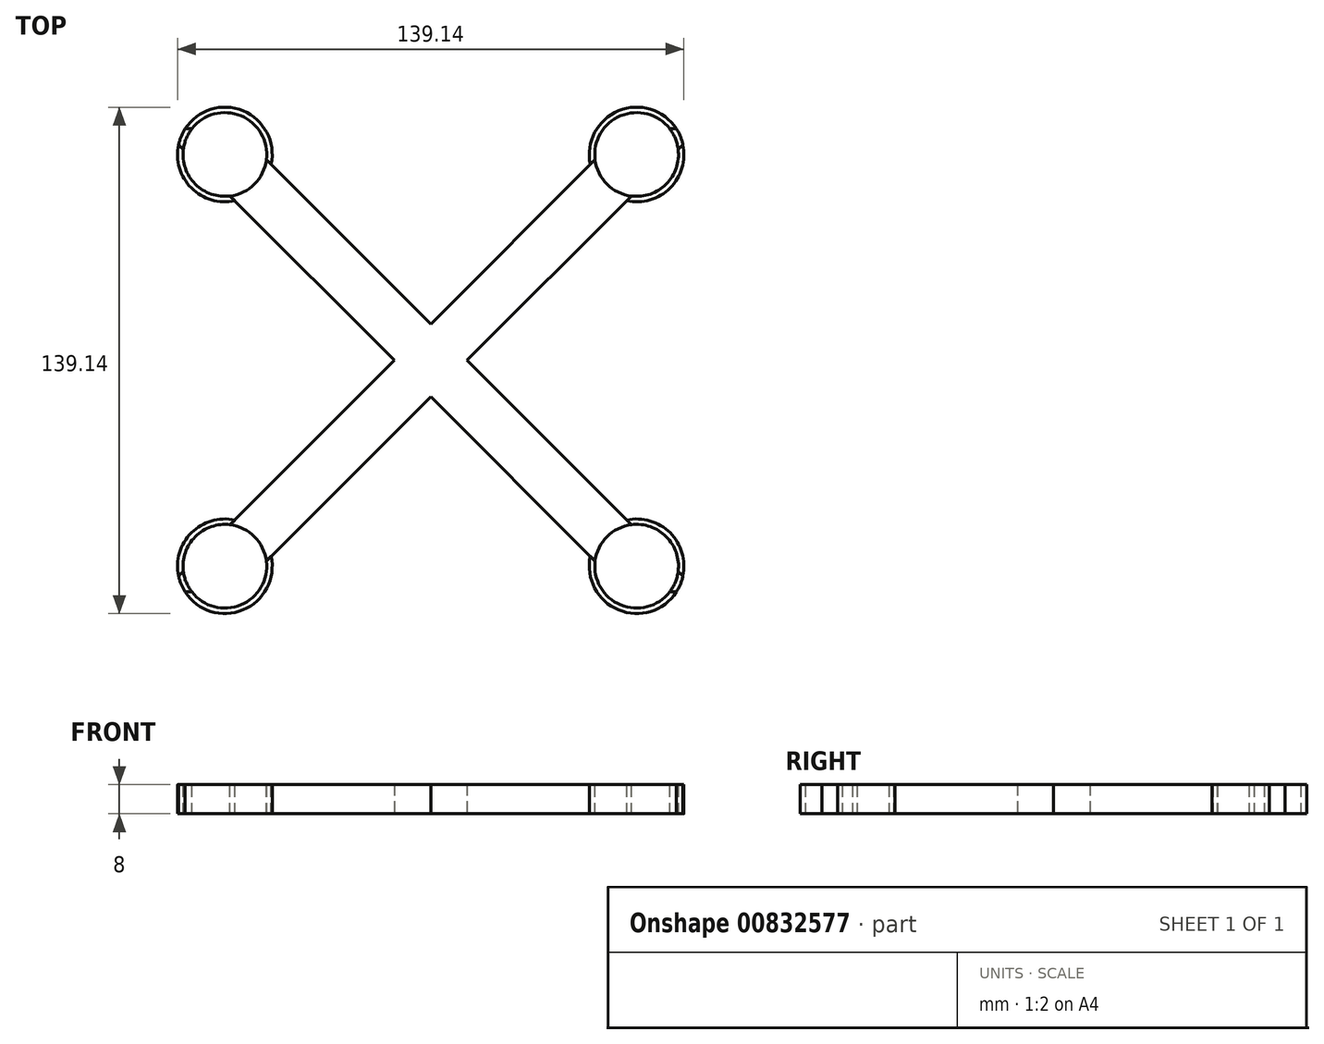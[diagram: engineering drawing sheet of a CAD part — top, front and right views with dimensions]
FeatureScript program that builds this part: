
annotation { "Feature Type Name" : "Feature", "Feature Type Description" : "" }
export const myFeature = defineFeature(function(context is Context, id is Id, definition is map)
    precondition{}
    {
        {
            var Q0;
            Q0=qCreatedBy(makeId("Top.planeOp"),FACE);
            var sketch = newSketch(context, id + "F0", { "sketchPlane" : qUnion([Q0])});
            skLineSegment(sketch, "E0", {"start": v(0, 0) * mm, "end": v(127.28, 127.28) * mm, "construction": true});
            skLineSegment(sketch, "E1", {"start": v(0, 127.28) * mm, "end": v(127.28, 0) * mm, "construction": true});
            skLineSegment(sketch, "E2", {"start": v(-10, 127.28) * mm, "end": v(10, 127.28) * mm});
            skLineSegment(sketch, "E3", {"start": v(117.28, 0) * mm, "end": v(137.28, 0) * mm});
            skLineSegment(sketch, "E4", {"start": v(10, 127.28) * mm, "end": v(137.28, 0) * mm});
            skLineSegment(sketch, "E5", {"start": v(117.28, 0) * mm, "end": v(-10, 127.28) * mm});
            skLineSegment(sketch, "E6", {"start": v(117.28, 127.28) * mm, "end": v(137.28, 127.28) * mm});
            skLineSegment(sketch, "E7", {"start": v(-10, 0) * mm, "end": v(10, 0) * mm});
            skLineSegment(sketch, "E8", {"start": v(-10, 0) * mm, "end": v(117.28, 127.28) * mm});
            skLineSegment(sketch, "E9", {"start": v(137.28, 127.28) * mm, "end": v(10, 0) * mm});
            skSolve(sketch);
        }
        {
            var Q0;
            {var subQ0=sQuery(id+"F0.wireOp",EDGE,"E2");Q0=makeQuery(id+"F0.imprint","IMPRINT",FACE,{"disambiguationData":[TD([[makeQuery(id+"F0.imprint","IMPRINT",EDGE,{"derivedFrom":subQ0}),-1.0]])]});}
            var Q1;
            {var subQ0=sQuery(id+"F0.wireOp",EDGE,"E8");var subQ1=sQuery(id+"F0.wireOp",EDGE,"E4");var subQ2=makeQuery(id+"F0.imprint","INTERSECT",VERTEX,{"derivedFrom":[subQ1,subQ0]});Q1=makeQuery(id+"F0.imprint","IMPRINT",FACE,{"disambiguationData":[TD([[makeQuery(id+"F0.imprint","IMPRINT",EDGE,{"disambiguationData":[TD([[subQ2,-1.0]])],"derivedFrom":subQ1}),-1.0]])]});}
            var Q2;
            {var subQ5=sQuery(id+"F0.wireOp",EDGE,"E6");Q2=makeQuery(id+"F0.imprint","IMPRINT",FACE,{"disambiguationData":[TD([[makeQuery(id+"F0.imprint","IMPRINT",EDGE,{"derivedFrom":subQ5}),-1.0]])]});}
            var Q3;
            {var subQ0=sQuery(id+"F0.wireOp",EDGE,"E3");Q3=makeQuery(id+"F0.imprint","IMPRINT",FACE,{"disambiguationData":[TD([[makeQuery(id+"F0.imprint","IMPRINT",EDGE,{"derivedFrom":subQ0}),1.0]])]});}
            var Q4;
            {var subQ5=sQuery(id+"F0.wireOp",EDGE,"E7");Q4=makeQuery(id+"F0.imprint","IMPRINT",FACE,{"disambiguationData":[TD([[makeQuery(id+"F0.imprint","IMPRINT",EDGE,{"derivedFrom":subQ5}),1.0]])]});}
            extrude(context, id + "F1", {"entities" : qUnion([Q0, Q1, Q2, Q3, Q4]), "depth" : 8 * mm, "offsetDistance" : 25 * mm});
        }
        {
            var Q0;
            Q0=makeQuery(id+"F1.opExtrude","CAP_FACE",FACE,{"disambiguationData":[OSD([sQuery(id+"F0.wireOp",EDGE,"E2"),sQuery(id+"F0.wireOp",EDGE,"E3"),sQuery(id+"F0.wireOp",EDGE,"E4"),sQuery(id+"F0.wireOp",EDGE,"E5"),sQuery(id+"F0.wireOp",EDGE,"E6"),sQuery(id+"F0.wireOp",EDGE,"E7"),sQuery(id+"F0.wireOp",EDGE,"E8"),sQuery(id+"F0.wireOp",EDGE,"E9")])],"isStart":false});
            var sketch = newSketch(context, id + "F2", { "sketchPlane" : qUnion([Q0])});
            skCircle(sketch, "E10", {"center": v(7.07, 7.07) * mm, "radius": 11.5 * mm});
            skCircle(sketch, "E11", {"center": v(120.2, 7.07) * mm, "radius": 11.5 * mm});
            skCircle(sketch, "E12", {"center": v(120.2, 120.2) * mm, "radius": 11.5 * mm});
            skCircle(sketch, "E13", {"center": v(7.07, 120.2) * mm, "radius": 11.5 * mm});
            skCircle(sketch, "E14", {"center": v(120.2, 120.2) * mm, "radius": 13 * mm});
            skCircle(sketch, "E15", {"center": v(120.2, 7.07) * mm, "radius": 13 * mm});
            skCircle(sketch, "E16", {"center": v(7.07, 7.07) * mm, "radius": 13 * mm});
            skCircle(sketch, "E17", {"center": v(7.07, 120.2) * mm, "radius": 13 * mm});
            skSolve(sketch);
        }
        {
            var Q0;
            Q0=makeQuery(id+"F2.imprint","IMPRINT",FACE,{"disambiguationData":[TD([[makeQuery(id+"F2.imprint","IMPRINT",EDGE,{"derivedFrom":sQuery(id+"F2.wireOp",EDGE,"E13")}),1.0]])]});
            var Q1;
            Q1=makeQuery(id+"F2.imprint","IMPRINT",FACE,{"disambiguationData":[TD([[makeQuery(id+"F2.imprint","IMPRINT",EDGE,{"derivedFrom":sQuery(id+"F2.wireOp",EDGE,"E11")}),1.0]])]});
            var Q2;
            Q2=makeQuery(id+"F2.imprint","IMPRINT",FACE,{"disambiguationData":[TD([[makeQuery(id+"F2.imprint","IMPRINT",EDGE,{"derivedFrom":sQuery(id+"F2.wireOp",EDGE,"E10")}),1.0]])]});
            extrude(context, id + "F3", {"entities" : qUnion([Q0, Q1, Q2]), "operationType" : NewBodyOperationType.REMOVE, "oppositeDirection" : true, "depth" : 25 * mm, "offsetDistance" : 25 * mm});
        }
        {
            var Q0;
            {var subQ1=sQuery(id+"F0.wireOp",EDGE,"E6");var subQ2=makeQuery(id+"F1.opExtrude","CAP_EDGE",EDGE,{"disambiguationData":[OSD([subQ1])],"isStart":false});var subQ7=sQuery(id+"F2.wireOp",EDGE,"E14");var subQ8=makeQuery(id+"F2.imprint","INTERSECT",VERTEX,{"derivedFrom":[subQ2,subQ7]});Q0=makeQuery(id+"F2.imprint","IMPRINT",FACE,{"disambiguationData":[TD([[makeQuery(id+"F2.imprint","IMPRINT",EDGE,{"disambiguationData":[TD([[subQ8,1.0]])],"derivedFrom":subQ2}),1.0]])]});}
            var Q1;
            {var subQ0=sQuery(id+"F2.wireOp",EDGE,"E12");var subQ1=sQuery(id+"F0.wireOp",EDGE,"E9");var subQ2=makeQuery(id+"F1.opExtrude","CAP_EDGE",EDGE,{"disambiguationData":[OSD([subQ1]),TDD([makeQuery(id+"F0.imprint","IMPRINT",EDGE,{"disambiguationData":[TD([[makeQuery(id+"F0.imprint","INTERSECT",VERTEX,{"derivedFrom":[sQuery(id+"F0.wireOp",EDGE,"E6"),subQ1]}),-1.0]])],"derivedFrom":subQ1})])],"isStart":false});var subQ3=makeQuery(id+"F2.imprint","INTERSECT",VERTEX,{"disambiguationData":[OD(0.0)],"derivedFrom":[subQ2,subQ0]});Q1=makeQuery(id+"F2.imprint","IMPRINT",FACE,{"disambiguationData":[TD([[makeQuery(id+"F2.imprint","IMPRINT",EDGE,{"disambiguationData":[TD([[subQ3,1.0]])],"derivedFrom":subQ0}),-1.0]])]});}
            var Q2;
            {var subQ1=sQuery(id+"F0.wireOp",EDGE,"E2");var subQ2=makeQuery(id+"F1.opExtrude","CAP_EDGE",EDGE,{"disambiguationData":[OSD([subQ1])],"isStart":false});var subQ7=sQuery(id+"F2.wireOp",EDGE,"E17");var subQ9=makeQuery(id+"F2.imprint","INTERSECT",VERTEX,{"derivedFrom":[subQ2,subQ7]});Q2=makeQuery(id+"F2.imprint","IMPRINT",FACE,{"disambiguationData":[TD([[makeQuery(id+"F2.imprint","IMPRINT",EDGE,{"disambiguationData":[TD([[subQ9,-1.0]])],"derivedFrom":subQ2}),1.0]])]});}
            var Q3;
            {var subQ0=sQuery(id+"F2.wireOp",EDGE,"E13");var subQ1=sQuery(id+"F0.wireOp",EDGE,"E5");var subQ2=makeQuery(id+"F1.opExtrude","CAP_EDGE",EDGE,{"disambiguationData":[OSD([subQ1]),TDD([makeQuery(id+"F0.imprint","IMPRINT",EDGE,{"disambiguationData":[TD([[makeQuery(id+"F0.imprint","INTERSECT",VERTEX,{"derivedFrom":[sQuery(id+"F0.wireOp",EDGE,"E2"),subQ1]}),1.0]])],"derivedFrom":subQ1})])],"isStart":false});var subQ3=makeQuery(id+"F2.imprint","INTERSECT",VERTEX,{"disambiguationData":[OD(0.0)],"derivedFrom":[subQ2,subQ0]});Q3=makeQuery(id+"F2.imprint","IMPRINT",FACE,{"disambiguationData":[TD([[makeQuery(id+"F2.imprint","IMPRINT",EDGE,{"disambiguationData":[TD([[subQ3,-1.0]])],"derivedFrom":subQ0}),-1.0]])]});}
            var Q4;
            {var subQ0=sQuery(id+"F2.wireOp",EDGE,"E10");var subQ1=sQuery(id+"F0.wireOp",EDGE,"E8");var subQ2=makeQuery(id+"F1.opExtrude","CAP_EDGE",EDGE,{"disambiguationData":[OSD([subQ1]),TDD([makeQuery(id+"F0.imprint","IMPRINT",EDGE,{"disambiguationData":[TD([[makeQuery(id+"F0.imprint","INTERSECT",VERTEX,{"derivedFrom":[sQuery(id+"F0.wireOp",EDGE,"E7"),subQ1]}),-1.0]])],"derivedFrom":subQ1})])],"isStart":false});var subQ3=makeQuery(id+"F2.imprint","INTERSECT",VERTEX,{"disambiguationData":[OD(0.0)],"derivedFrom":[subQ2,subQ0]});Q4=makeQuery(id+"F2.imprint","IMPRINT",FACE,{"disambiguationData":[TD([[makeQuery(id+"F2.imprint","IMPRINT",EDGE,{"disambiguationData":[TD([[subQ3,-1.0]])],"derivedFrom":subQ0}),-1.0]])]});}
            var Q5;
            {var subQ2=sQuery(id+"F0.wireOp",EDGE,"E7");var subQ5=makeQuery(id+"F1.opExtrude","CAP_EDGE",EDGE,{"disambiguationData":[OSD([subQ2])],"isStart":false});var subQ7=sQuery(id+"F2.wireOp",EDGE,"E16");var subQ8=makeQuery(id+"F2.imprint","INTERSECT",VERTEX,{"derivedFrom":[subQ5,subQ7]});Q5=makeQuery(id+"F2.imprint","IMPRINT",FACE,{"disambiguationData":[TD([[makeQuery(id+"F2.imprint","IMPRINT",EDGE,{"disambiguationData":[TD([[subQ8,-1.0]])],"derivedFrom":subQ5}),-1.0]])]});}
            var Q6;
            {var subQ2=sQuery(id+"F0.wireOp",EDGE,"E3");var subQ5=makeQuery(id+"F1.opExtrude","CAP_EDGE",EDGE,{"disambiguationData":[OSD([subQ2])],"isStart":false});var subQ7=sQuery(id+"F2.wireOp",EDGE,"E15");var subQ9=makeQuery(id+"F2.imprint","INTERSECT",VERTEX,{"derivedFrom":[subQ5,subQ7]});Q6=makeQuery(id+"F2.imprint","IMPRINT",FACE,{"disambiguationData":[TD([[makeQuery(id+"F2.imprint","IMPRINT",EDGE,{"disambiguationData":[TD([[subQ9,1.0]])],"derivedFrom":subQ5}),-1.0]])]});}
            var Q7;
            {var subQ0=sQuery(id+"F2.wireOp",EDGE,"E11");var subQ1=sQuery(id+"F0.wireOp",EDGE,"E4");var subQ2=makeQuery(id+"F1.opExtrude","CAP_EDGE",EDGE,{"disambiguationData":[OSD([subQ1]),TDD([makeQuery(id+"F0.imprint","IMPRINT",EDGE,{"disambiguationData":[TD([[makeQuery(id+"F0.imprint","INTERSECT",VERTEX,{"derivedFrom":[sQuery(id+"F0.wireOp",EDGE,"E3"),subQ1]}),1.0]])],"derivedFrom":subQ1})])],"isStart":false});var subQ3=makeQuery(id+"F2.imprint","INTERSECT",VERTEX,{"disambiguationData":[OD(0.0)],"derivedFrom":[subQ2,subQ0]});Q7=makeQuery(id+"F2.imprint","IMPRINT",FACE,{"disambiguationData":[TD([[makeQuery(id+"F2.imprint","IMPRINT",EDGE,{"disambiguationData":[TD([[subQ3,1.0]])],"derivedFrom":subQ0}),-1.0]])]});}
            extrude(context, id + "F4", {"entities" : qUnion([Q0, Q1, Q2, Q3, Q4, Q5, Q6, Q7]), "oppositeDirection" : true, "depth" : 8 * mm, "offsetDistance" : 25 * mm});
        }
        {
            var Q0;
            {var subQ1=sQuery(id+"F0.wireOp",EDGE,"E6");var subQ4=makeQuery(id+"F1.opExtrude","CAP_EDGE",EDGE,{"disambiguationData":[OSD([subQ1])],"isStart":false});var subQ6=sQuery(id+"F2.wireOp",EDGE,"E12");var subQ7=makeQuery(id+"F2.imprint","INTERSECT",VERTEX,{"derivedFrom":[subQ4,subQ6]});Q0=makeQuery(id+"F2.imprint","IMPRINT",FACE,{"disambiguationData":[TD([[makeQuery(id+"F2.imprint","IMPRINT",EDGE,{"disambiguationData":[TD([[subQ7,1.0]])],"derivedFrom":subQ6}),1.0]])]});}
            var Q1;
            {var subQ0=sQuery(id+"F2.wireOp",EDGE,"E14");var subQ1=sQuery(id+"F0.wireOp",EDGE,"E6");var subQ2=makeQuery(id+"F1.opExtrude","CAP_EDGE",EDGE,{"disambiguationData":[OSD([subQ1])],"isStart":false});var subQ3=makeQuery(id+"F2.imprint","INTERSECT",VERTEX,{"derivedFrom":[subQ2,subQ0]});Q1=makeQuery(id+"F2.imprint","IMPRINT",FACE,{"disambiguationData":[TD([[makeQuery(id+"F2.imprint","IMPRINT",EDGE,{"disambiguationData":[TD([[subQ3,1.0]])],"derivedFrom":subQ0}),-1.0]])]});}
            var Q2;
            {var subQ0=sQuery(id+"F2.wireOp",EDGE,"E17");var subQ2=sQuery(id+"F0.wireOp",EDGE,"E2");var subQ5=makeQuery(id+"F1.opExtrude","CAP_EDGE",EDGE,{"disambiguationData":[OSD([subQ2])],"isStart":false});var subQ6=makeQuery(id+"F2.imprint","INTERSECT",VERTEX,{"derivedFrom":[subQ5,subQ0]});Q2=makeQuery(id+"F2.imprint","IMPRINT",FACE,{"disambiguationData":[TD([[makeQuery(id+"F2.imprint","IMPRINT",EDGE,{"disambiguationData":[TD([[subQ6,-1.0]])],"derivedFrom":subQ0}),-1.0]])]});}
            var Q3;
            {var subQ0=sQuery(id+"F2.wireOp",EDGE,"E16");var subQ2=sQuery(id+"F0.wireOp",EDGE,"E7");var subQ5=makeQuery(id+"F1.opExtrude","CAP_EDGE",EDGE,{"disambiguationData":[OSD([subQ2])],"isStart":false});var subQ6=makeQuery(id+"F2.imprint","INTERSECT",VERTEX,{"derivedFrom":[subQ5,subQ0]});Q3=makeQuery(id+"F2.imprint","IMPRINT",FACE,{"disambiguationData":[TD([[makeQuery(id+"F2.imprint","IMPRINT",EDGE,{"disambiguationData":[TD([[subQ6,1.0]])],"derivedFrom":subQ0}),-1.0]])]});}
            var Q4;
            {var subQ0=sQuery(id+"F2.wireOp",EDGE,"E15");var subQ1=sQuery(id+"F0.wireOp",EDGE,"E3");var subQ2=makeQuery(id+"F1.opExtrude","CAP_EDGE",EDGE,{"disambiguationData":[OSD([subQ1])],"isStart":false});var subQ3=makeQuery(id+"F2.imprint","INTERSECT",VERTEX,{"derivedFrom":[subQ2,subQ0]});Q4=makeQuery(id+"F2.imprint","IMPRINT",FACE,{"disambiguationData":[TD([[makeQuery(id+"F2.imprint","IMPRINT",EDGE,{"disambiguationData":[TD([[subQ3,-1.0]])],"derivedFrom":subQ0}),-1.0]])]});}
            extrude(context, id + "F5", {"entities" : qUnion([Q0, Q1, Q2, Q3, Q4]), "operationType" : NewBodyOperationType.REMOVE, "oppositeDirection" : true, "depth" : 25 * mm, "offsetDistance" : 25 * mm});
        }
    });
